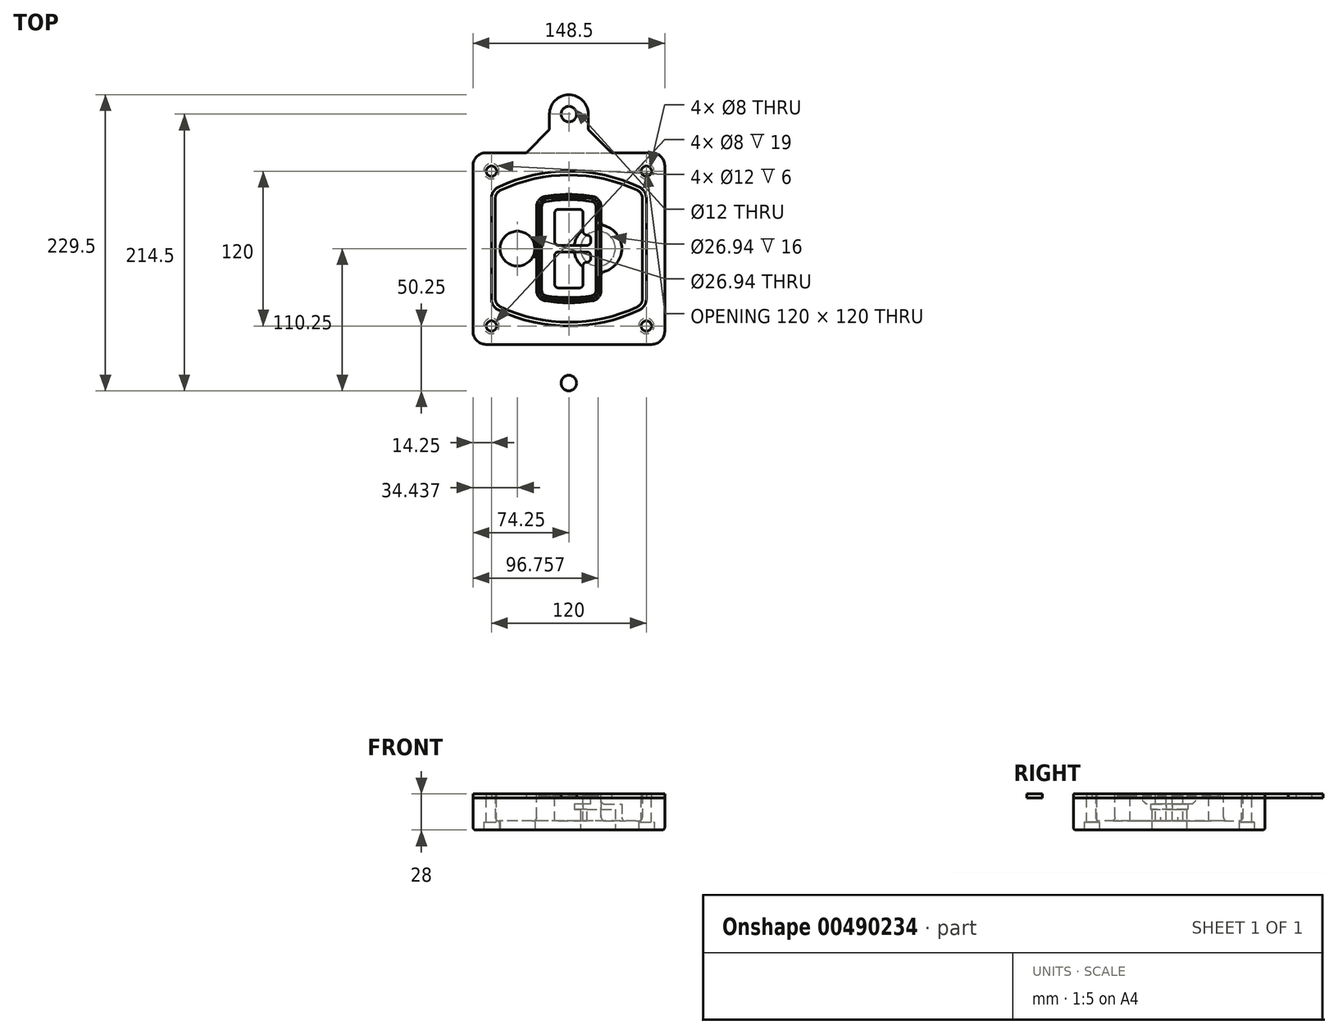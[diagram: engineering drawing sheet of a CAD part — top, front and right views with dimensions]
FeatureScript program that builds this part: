
annotation { "Feature Type Name" : "Feature", "Feature Type Description" : "" }
export const myFeature = defineFeature(function(context is Context, id is Id, definition is map)
    precondition{}
    {
        {
            var Q0;
            Q0=qCreatedBy(makeId("Top.planeOp"),FACE);
            var sketch = newSketch(context, id + "F0", { "sketchPlane" : qUnion([Q0])});
            skPoint(sketch, "E0.rect.middle", {"position": v(0, 0) * mm});
            skLineSegment(sketch, "E1.bottom", {"start": v(-64.25, -74.25) * mm, "end": v(64.25, -74.25) * mm});
            skLineSegment(sketch, "E1.top", {"start": v(-64.25, 74.25) * mm, "end": v(64.25, 74.25) * mm});
            skLineSegment(sketch, "E1.left", {"start": v(-74.25, -64.25) * mm, "end": v(-74.25, 64.25) * mm});
            skLineSegment(sketch, "E1.right", {"start": v(74.25, -64.25) * mm, "end": v(74.25, 64.25) * mm});
            skLineSegment(sketch, "E2", {"start": v(-74.25, 74.25) * mm, "end": v(74.25, -74.25) * mm, "construction": true});
            skLineSegment(sketch, "E3", {"start": v(74.25, 74.25) * mm, "end": v(-74.25, -74.25) * mm, "construction": true});
            skCircle(sketch, "E4", {"center": v(-60, 60) * mm, "radius": 4 * mm});
            skCircle(sketch, "E5", {"center": v(60, 60) * mm, "radius": 4 * mm});
            skCircle(sketch, "E6", {"center": v(60, -60) * mm, "radius": 4 * mm});
            skCircle(sketch, "E7", {"center": v(-60, -60) * mm, "radius": 4 * mm});
            skLineSegment(sketch, "E8", {"start": v(-60, 60) * mm, "end": v(60, 60) * mm, "construction": true});
            skLineSegment(sketch, "E9", {"start": v(60, 60) * mm, "end": v(60, -60) * mm, "construction": true});
            skLineSegment(sketch, "E10", {"start": v(60, -60) * mm, "end": v(-60, -60) * mm, "construction": true});
            skLineSegment(sketch, "E11", {"start": v(-60, -60) * mm, "end": v(-60, 60) * mm, "construction": true});
            skLineSegment(sketch, "E12", {"start": v(-60, 38.83) * mm, "end": v(-60, -38.83) * mm});
            skLineSegment(sketch, "E13", {"start": v(60, 38.83) * mm, "end": v(60, -38.83) * mm});
            skArc(sketch, "E14", {"start": v(54.26, 47.88) * mm, "mid": v(0, 60) * mm, "end": v(-54.26, 47.88) * mm});
            skArc(sketch, "E15", {"start": v(-54.26, -47.88) * mm, "mid": v(0, -60) * mm, "end": v(54.26, -47.88) * mm});
            skLineSegment(sketch, "E16", {"start": v(-60, 0) * mm, "end": v(60, 0) * mm, "construction": true});
            skPoint(sketch, "E17.visualSharp", {"position": v(-60, -45) * mm});
            skArc(sketch, "E17.filletArc", {"start": v(-60, -38.83) * mm, "mid": v(-58.44, -44.2) * mm, "end": v(-54.26, -47.88) * mm});
            skPoint(sketch, "E18.visualSharp", {"position": v(-60, 45) * mm});
            skArc(sketch, "E18.filletArc", {"start": v(-54.26, 47.88) * mm, "mid": v(-58.44, 44.2) * mm, "end": v(-60, 38.83) * mm});
            skPoint(sketch, "E19.visualSharp", {"position": v(60, 45) * mm});
            skArc(sketch, "E19.filletArc", {"start": v(60, 38.83) * mm, "mid": v(58.44, 44.2) * mm, "end": v(54.26, 47.88) * mm});
            skPoint(sketch, "E20.visualSharp", {"position": v(60, -45) * mm});
            skArc(sketch, "E20.filletArc", {"start": v(54.26, -47.88) * mm, "mid": v(58.44, -44.2) * mm, "end": v(60, -38.83) * mm});
            skPoint(sketch, "E21.visualSharp", {"position": v(-74.25, 74.25) * mm});
            skArc(sketch, "E21.filletArc", {"start": v(-64.25, 74.25) * mm, "mid": v(-71.32, 71.32) * mm, "end": v(-74.25, 64.25) * mm});
            skPoint(sketch, "E22.visualSharp", {"position": v(74.25, 74.25) * mm});
            skArc(sketch, "E22.filletArc", {"start": v(74.25, 64.25) * mm, "mid": v(71.32, 71.32) * mm, "end": v(64.25, 74.25) * mm});
            skPoint(sketch, "E23.visualSharp", {"position": v(74.25, -74.25) * mm});
            skArc(sketch, "E23.filletArc", {"start": v(64.25, -74.25) * mm, "mid": v(71.32, -71.32) * mm, "end": v(74.25, -64.25) * mm});
            skPoint(sketch, "E24.visualSharp", {"position": v(-74.25, -74.25) * mm});
            skArc(sketch, "E24.filletArc", {"start": v(-74.25, -64.25) * mm, "mid": v(-71.32, -71.32) * mm, "end": v(-64.25, -74.25) * mm});
            skArc(sketch, "E25.0", {"start": v(57, 38.83) * mm, "mid": v(55.9, 42.58) * mm, "end": v(52.98, 45.17) * mm});
            skLineSegment(sketch, "E25.1", {"start": v(57, 38.83) * mm, "end": v(57, -38.83) * mm});
            skArc(sketch, "E25.2", {"start": v(52.98, -45.17) * mm, "mid": v(55.9, -42.58) * mm, "end": v(57, -38.83) * mm});
            skArc(sketch, "E25.3", {"start": v(-52.98, -45.17) * mm, "mid": v(0, -57) * mm, "end": v(52.98, -45.17) * mm});
            skArc(sketch, "E25.4", {"start": v(-57, -38.83) * mm, "mid": v(-55.9, -42.58) * mm, "end": v(-52.98, -45.17) * mm});
            skArc(sketch, "E25.5", {"start": v(52.98, 45.17) * mm, "mid": v(0, 57) * mm, "end": v(-52.98, 45.17) * mm});
            skLineSegment(sketch, "E25.6", {"start": v(-57, 38.83) * mm, "end": v(-57, -38.83) * mm});
            skArc(sketch, "E25.7", {"start": v(-52.98, 45.17) * mm, "mid": v(-55.9, 42.58) * mm, "end": v(-57, 38.83) * mm});
            skArc(sketch, "E26.0", {"start": v(-55.96, 51.5) * mm, "mid": v(-61.82, 46.33) * mm, "end": v(-64, 38.83) * mm});
            skArc(sketch, "E26.1", {"start": v(55.96, 51.5) * mm, "mid": v(0, 64) * mm, "end": v(-55.96, 51.5) * mm});
            skArc(sketch, "E26.2", {"start": v(64, 38.83) * mm, "mid": v(61.82, 46.33) * mm, "end": v(55.96, 51.5) * mm});
            skLineSegment(sketch, "E26.3", {"start": v(64, 38.83) * mm, "end": v(64, -38.83) * mm});
            skArc(sketch, "E26.4", {"start": v(55.96, -51.5) * mm, "mid": v(61.82, -46.33) * mm, "end": v(64, -38.83) * mm});
            skLineSegment(sketch, "E26.5", {"start": v(-64, 38.83) * mm, "end": v(-64, -38.83) * mm});
            skArc(sketch, "E26.6", {"start": v(-55.96, -51.5) * mm, "mid": v(0, -64) * mm, "end": v(55.96, -51.5) * mm});
            skArc(sketch, "E26.7", {"start": v(-64, -38.83) * mm, "mid": v(-61.82, -46.33) * mm, "end": v(-55.96, -51.5) * mm});
            skSolve(sketch);
        }
        {
            var Q0;
            Q0=makeQuery(id+"F0.imprint","IMPRINT",FACE,{"disambiguationData":[TD([[makeQuery(id+"F0.imprint","IMPRINT",EDGE,{"derivedFrom":sQuery(id+"F0.wireOp",EDGE,"E1.bottom")}),1.0]])]});
            var Q1;
            Q1=makeQuery(id+"F0.imprint","IMPRINT",FACE,{"disambiguationData":[TD([[makeQuery(id+"F0.imprint","IMPRINT",EDGE,{"derivedFrom":sQuery(id+"F0.wireOp",EDGE,"E12")}),1.0]])]});
            var Q2;
            Q2=makeQuery(id+"F0.imprint","IMPRINT",FACE,{"disambiguationData":[TD([[makeQuery(id+"F0.imprint","IMPRINT",EDGE,{"derivedFrom":sQuery(id+"F0.wireOp",EDGE,"E25.0")}),1.0]])]});
            var Q3;
            Q3=makeQuery(id+"F0.imprint","IMPRINT",FACE,{"disambiguationData":[TD([[makeQuery(id+"F0.imprint","IMPRINT",EDGE,{"derivedFrom":sQuery(id+"F0.wireOp",EDGE,"E12")}),-1.0]])]});
            extrude(context, id + "F1", {"entities" : qUnion([Q0, Q1, Q2, Q3]), "oppositeDirection" : true, "depth" : 25 * mm});
        }
        {
            var Q0;
            Q0=makeQuery(id+"F0.imprint","IMPRINT",FACE,{"disambiguationData":[TD([[makeQuery(id+"F0.imprint","IMPRINT",EDGE,{"derivedFrom":sQuery(id+"F0.wireOp",EDGE,"E12")}),1.0]])]});
            extrude(context, id + "F2", {"entities" : qUnion([Q0]), "operationType" : NewBodyOperationType.ADD, "depth" : 3 * mm});
        }
        {
            var Q0;
            Q0=makeQuery(id+"F0.imprint","IMPRINT",FACE,{"disambiguationData":[TD([[makeQuery(id+"F0.imprint","IMPRINT",EDGE,{"derivedFrom":sQuery(id+"F0.wireOp",EDGE,"E25.0")}),1.0]])]});
            extrude(context, id + "F3", {"entities" : qUnion([Q0]), "operationType" : NewBodyOperationType.REMOVE, "oppositeDirection" : true, "depth" : 18 * mm});
        }
        {
            var Q0;
            Q0=makeQuery(id+"F2.opExtrude","CAP_FACE",FACE,{"disambiguationData":[OSD([sQuery(id+"F0.wireOp",EDGE,"E12"),sQuery(id+"F0.wireOp",EDGE,"E13"),sQuery(id+"F0.wireOp",EDGE,"E14"),sQuery(id+"F0.wireOp",EDGE,"E15"),sQuery(id+"F0.wireOp",EDGE,"E17.filletArc"),sQuery(id+"F0.wireOp",EDGE,"E18.filletArc"),sQuery(id+"F0.wireOp",EDGE,"E19.filletArc"),sQuery(id+"F0.wireOp",EDGE,"E20.filletArc"),sQuery(id+"F0.wireOp",EDGE,"E25.0"),sQuery(id+"F0.wireOp",EDGE,"E25.1"),sQuery(id+"F0.wireOp",EDGE,"E25.2"),sQuery(id+"F0.wireOp",EDGE,"E25.3"),sQuery(id+"F0.wireOp",EDGE,"E25.4"),sQuery(id+"F0.wireOp",EDGE,"E25.5"),sQuery(id+"F0.wireOp",EDGE,"E25.6"),sQuery(id+"F0.wireOp",EDGE,"E25.7")])],"isStart":false});
            var sketch = newSketch(context, id + "F4", { "sketchPlane" : qUnion([Q0])});
            skArc(sketch, "E27.0", {"start": v(-18.34, -40.45) * mm, "mid": v(0, -42) * mm, "end": v(18.34, -40.45) * mm});
            skArc(sketch, "E28.0", {"start": v(18.34, 40.45) * mm, "mid": v(0, 42) * mm, "end": v(-18.34, 40.45) * mm});
            skLineSegment(sketch, "E29", {"start": v(-25, 32.57) * mm, "end": v(-25, -32.57) * mm});
            skLineSegment(sketch, "E30", {"start": v(25, 32.57) * mm, "end": v(25, -32.57) * mm});
            skLineSegment(sketch, "E31", {"start": v(-25, 39.1) * mm, "end": v(25, 39.1) * mm, "construction": true});
            skLineSegment(sketch, "E32", {"start": v(-25, -39.1) * mm, "end": v(25, -39.1) * mm, "construction": true});
            skPoint(sketch, "E33.visualSharp", {"position": v(-25, 39.1) * mm});
            skArc(sketch, "E33.filletArc", {"start": v(-18.34, 40.45) * mm, "mid": v(-23.11, 37.73) * mm, "end": v(-25, 32.57) * mm});
            skPoint(sketch, "E34.visualSharp", {"position": v(25, 39.1) * mm});
            skArc(sketch, "E34.filletArc", {"start": v(25, 32.57) * mm, "mid": v(23.11, 37.73) * mm, "end": v(18.34, 40.45) * mm});
            skPoint(sketch, "E35.visualSharp", {"position": v(25, -39.1) * mm});
            skArc(sketch, "E35.filletArc", {"start": v(18.34, -40.45) * mm, "mid": v(23.11, -37.73) * mm, "end": v(25, -32.57) * mm});
            skPoint(sketch, "E36.visualSharp", {"position": v(-25, -39.1) * mm});
            skArc(sketch, "E36.filletArc", {"start": v(-25, -32.57) * mm, "mid": v(-23.11, -37.73) * mm, "end": v(-18.34, -40.45) * mm});
            skArc(sketch, "E37.0", {"start": v(52.98, 45.17) * mm, "mid": v(0, 57) * mm, "end": v(-52.98, 45.17) * mm});
            skArc(sketch, "E37.1", {"start": v(-52.98, 45.17) * mm, "mid": v(-55.9, 42.58) * mm, "end": v(-57, 38.83) * mm});
            skLineSegment(sketch, "E37.2", {"start": v(-57, 38.83) * mm, "end": v(-57, -38.83) * mm});
            skArc(sketch, "E37.3", {"start": v(-57, -38.83) * mm, "mid": v(-55.9, -42.58) * mm, "end": v(-52.98, -45.17) * mm});
            skArc(sketch, "E37.4", {"start": v(-52.98, -45.17) * mm, "mid": v(0, -57) * mm, "end": v(52.98, -45.17) * mm});
            skArc(sketch, "E37.5", {"start": v(52.98, -45.17) * mm, "mid": v(55.9, -42.58) * mm, "end": v(57, -38.83) * mm});
            skLineSegment(sketch, "E37.6", {"start": v(57, 38.83) * mm, "end": v(57, -38.83) * mm});
            skArc(sketch, "E37.7", {"start": v(57, 38.83) * mm, "mid": v(55.9, 42.58) * mm, "end": v(52.98, 45.17) * mm});
            skLineSegment(sketch, "E38.0", {"start": v(23, 32.57) * mm, "end": v(23, -32.57) * mm});
            skArc(sketch, "E38.1", {"start": v(18, -38.48) * mm, "mid": v(21.58, -36.44) * mm, "end": v(23, -32.57) * mm});
            skArc(sketch, "E38.2", {"start": v(-18, -38.48) * mm, "mid": v(0, -40) * mm, "end": v(18, -38.48) * mm});
            skArc(sketch, "E38.3", {"start": v(-23, -32.57) * mm, "mid": v(-21.58, -36.44) * mm, "end": v(-18, -38.48) * mm});
            skLineSegment(sketch, "E38.4", {"start": v(-23, 32.57) * mm, "end": v(-23, -32.57) * mm});
            skArc(sketch, "E38.5", {"start": v(23, 32.57) * mm, "mid": v(21.58, 36.44) * mm, "end": v(18, 38.48) * mm});
            skArc(sketch, "E38.6", {"start": v(-18, 38.48) * mm, "mid": v(-21.58, 36.44) * mm, "end": v(-23, 32.57) * mm});
            skArc(sketch, "E38.7", {"start": v(18, 38.48) * mm, "mid": v(0, 40) * mm, "end": v(-18, 38.48) * mm});
            skArc(sketch, "E39.0", {"start": v(21, 32.57) * mm, "mid": v(20.06, 35.15) * mm, "end": v(17.67, 36.5) * mm});
            skLineSegment(sketch, "E39.1", {"start": v(21, 32.57) * mm, "end": v(21, -32.57) * mm});
            skArc(sketch, "E39.2", {"start": v(17.67, -36.5) * mm, "mid": v(20.06, -35.15) * mm, "end": v(21, -32.57) * mm});
            skArc(sketch, "E39.3", {"start": v(-17.67, -36.5) * mm, "mid": v(0, -38) * mm, "end": v(17.67, -36.5) * mm});
            skArc(sketch, "E39.4", {"start": v(-21, -32.57) * mm, "mid": v(-20.06, -35.15) * mm, "end": v(-17.67, -36.5) * mm});
            skArc(sketch, "E39.5", {"start": v(17.67, 36.5) * mm, "mid": v(0, 38) * mm, "end": v(-17.67, 36.5) * mm});
            skLineSegment(sketch, "E39.6", {"start": v(-21, 32.57) * mm, "end": v(-21, -32.57) * mm});
            skArc(sketch, "E39.7", {"start": v(-17.67, 36.5) * mm, "mid": v(-20.06, 35.15) * mm, "end": v(-21, 32.57) * mm});
            skLineSegment(sketch, "E40", {"start": v(-25, 0) * mm, "end": v(25, 0) * mm, "construction": true});
            skLineSegment(sketch, "E41", {"start": v(-11, 5.5) * mm, "end": v(-11, 27.5) * mm});
            skLineSegment(sketch, "E42", {"start": v(-8, 30.5) * mm, "end": v(8, 30.5) * mm});
            skLineSegment(sketch, "E43", {"start": v(11, 27.5) * mm, "end": v(11, 13.5) * mm});
            skLineSegment(sketch, "E44", {"start": v(14, 10.5) * mm, "end": v(14, 10.5) * mm});
            skLineSegment(sketch, "E45", {"start": v(17, 7.5) * mm, "end": v(17, 5.5) * mm});
            skLineSegment(sketch, "E46", {"start": v(14, 2.5) * mm, "end": v(-8, 2.5) * mm});
            skPoint(sketch, "E47.visualSharp", {"position": v(-11, 30.5) * mm});
            skArc(sketch, "E47.filletArc", {"start": v(-8, 30.5) * mm, "mid": v(-10.12, 29.62) * mm, "end": v(-11, 27.5) * mm});
            skPoint(sketch, "E48.visualSharp", {"position": v(11, 30.5) * mm});
            skArc(sketch, "E48.filletArc", {"start": v(11, 27.5) * mm, "mid": v(10.12, 29.62) * mm, "end": v(8, 30.5) * mm});
            skPoint(sketch, "E49.visualSharp", {"position": v(11, 10.5) * mm});
            skArc(sketch, "E49.filletArc", {"start": v(11, 13.5) * mm, "mid": v(11.88, 11.38) * mm, "end": v(14, 10.5) * mm});
            skPoint(sketch, "E50.visualSharp", {"position": v(17, 10.5) * mm});
            skArc(sketch, "E50.filletArc", {"start": v(17, 7.5) * mm, "mid": v(16.12, 9.62) * mm, "end": v(14, 10.5) * mm});
            skPoint(sketch, "E51.visualSharp", {"position": v(17, 2.5) * mm});
            skArc(sketch, "E51.filletArc", {"start": v(14, 2.5) * mm, "mid": v(16.12, 3.38) * mm, "end": v(17, 5.5) * mm});
            skPoint(sketch, "E52.visualSharp", {"position": v(-11, 2.5) * mm});
            skArc(sketch, "E52.filletArc", {"start": v(-11, 5.5) * mm, "mid": v(-10.12, 3.38) * mm, "end": v(-8, 2.5) * mm});
            skLineSegment(sketch, "E53.0.MirrorCS", {"start": v(14, -2.5) * mm, "end": v(-8, -2.5) * mm});
            skArc(sketch, "E54.0.MirrorCS", {"start": v(-11, -5.5) * mm, "mid": v(-10.12, -3.38) * mm, "end": v(-8, -2.5) * mm});
            skLineSegment(sketch, "E55.0.MirrorCS", {"start": v(-11, -5.5) * mm, "end": v(-11, -27.5) * mm});
            skArc(sketch, "E56.0.MirrorCS", {"start": v(-8, -30.5) * mm, "mid": v(-10.12, -29.62) * mm, "end": v(-11, -27.5) * mm});
            skLineSegment(sketch, "E57.0.MirrorCS", {"start": v(-8, -30.5) * mm, "end": v(8, -30.5) * mm});
            skArc(sketch, "E58.0.MirrorCS", {"start": v(11, -27.5) * mm, "mid": v(10.12, -29.62) * mm, "end": v(8, -30.5) * mm});
            skLineSegment(sketch, "E59.0.MirrorCS", {"start": v(11, -27.5) * mm, "end": v(11, -13.5) * mm});
            skArc(sketch, "E60.0.MirrorCS", {"start": v(11, -13.5) * mm, "mid": v(11.88, -11.38) * mm, "end": v(14, -10.5) * mm});
            skArc(sketch, "E61.0.MirrorCS", {"start": v(17, -7.5) * mm, "mid": v(16.12, -9.62) * mm, "end": v(14, -10.5) * mm});
            skLineSegment(sketch, "E62.0.MirrorCS", {"start": v(17, -7.5) * mm, "end": v(17, -5.5) * mm});
            skArc(sketch, "E63.0.MirrorCS", {"start": v(14, -2.5) * mm, "mid": v(16.12, -3.38) * mm, "end": v(17, -5.5) * mm});
            skSolve(sketch);
        }
        {
            var Q0;
            Q0=makeQuery(id+"F4.imprint","IMPRINT",FACE,{"disambiguationData":[TD([[makeQuery(id+"F4.imprint","IMPRINT",EDGE,{"derivedFrom":sQuery(id+"F4.wireOp",EDGE,"E27.0")}),1.0]])]});
            var Q1;
            Q1=makeQuery(id+"F4.imprint","IMPRINT",FACE,{"disambiguationData":[TD([[makeQuery(id+"F4.imprint","IMPRINT",EDGE,{"derivedFrom":sQuery(id+"F4.wireOp",EDGE,"E38.0")}),-1.0]])]});
            var Q2;
            Q2=makeQuery(id+"F4.imprint","IMPRINT",FACE,{"disambiguationData":[TD([[makeQuery(id+"F4.imprint","IMPRINT",EDGE,{"derivedFrom":sQuery(id+"F4.wireOp",EDGE,"E39.0")}),1.0]])]});
            extrude(context, id + "F5", {"entities" : qUnion([Q0, Q1, Q2]), "operationType" : NewBodyOperationType.ADD, "endBound" : BoundingType.UP_TO_NEXT, "oppositeDirection" : true, "depth" : 25 * mm});
        }
        {
            var Q0;
            Q0=makeQuery(id+"F4.imprint","IMPRINT",FACE,{"disambiguationData":[TD([[makeQuery(id+"F4.imprint","IMPRINT",EDGE,{"derivedFrom":sQuery(id+"F4.wireOp",EDGE,"E38.0")}),-1.0]])]});
            extrude(context, id + "F6", {"entities" : qUnion([Q0]), "operationType" : NewBodyOperationType.REMOVE, "oppositeDirection" : true, "depth" : 2 * mm});
        }
        {
            var Q0;
            Q0=makeQuery(id+"F1.opExtrude","CAP_FACE",FACE,{"disambiguationData":[OSD([sQuery(id+"F0.wireOp",EDGE,"E1.bottom"),sQuery(id+"F0.wireOp",EDGE,"E1.top"),sQuery(id+"F0.wireOp",EDGE,"E1.left"),sQuery(id+"F0.wireOp",EDGE,"E1.right"),sQuery(id+"F0.wireOp",EDGE,"E4"),sQuery(id+"F0.wireOp",EDGE,"E5"),sQuery(id+"F0.wireOp",EDGE,"E6"),sQuery(id+"F0.wireOp",EDGE,"E7"),sQuery(id+"F0.wireOp",EDGE,"E21.filletArc"),sQuery(id+"F0.wireOp",EDGE,"E22.filletArc"),sQuery(id+"F0.wireOp",EDGE,"E23.filletArc"),sQuery(id+"F0.wireOp",EDGE,"E24.filletArc")])],"isStart":false});
            var sketch = newSketch(context, id + "F7", { "sketchPlane" : qUnion([Q0])});
            skCircle(sketch, "E64", {"center": v(22.5, 0) * mm, "radius": 13.47 * mm});
            skCircle(sketch, "E65", {"center": v(-39.81, 0) * mm, "radius": 13.47 * mm});
            skLineSegment(sketch, "E66", {"start": v(74.25, 0) * mm, "end": v(-74.25, 0) * mm});
            skCircle(sketch, "E67", {"center": v(22.5, 0) * mm, "radius": 18.47 * mm});
            skCircle(sketch, "E68", {"center": v(60, -60) * mm, "radius": 6 * mm});
            skCircle(sketch, "E69", {"center": v(-60, -60) * mm, "radius": 6 * mm});
            skCircle(sketch, "E70", {"center": v(-60, 60) * mm, "radius": 6 * mm});
            skCircle(sketch, "E71", {"center": v(60, 60) * mm, "radius": 6 * mm});
            skSolve(sketch);
        }
        {
            var Q0;
            {var subQ1=sQuery(id+"F7.wireOp",EDGE,"E66");var subQ4=sQuery(id+"F7.wireOp",EDGE,"E64");var subQ6=makeQuery(id+"F7.imprint","INTERSECT",VERTEX,{"disambiguationData":[OD(0.0)],"derivedFrom":[subQ4,subQ1]});Q0=makeQuery(id+"F7.imprint","IMPRINT",FACE,{"disambiguationData":[TD([[makeQuery(id+"F7.imprint","IMPRINT",EDGE,{"disambiguationData":[TD([[subQ6,-1.0]])],"derivedFrom":subQ4}),-1.0]])]});}
            var Q1;
            {var subQ0=sQuery(id+"F7.wireOp",EDGE,"E66");var subQ1=sQuery(id+"F7.wireOp",EDGE,"E64");var subQ3=makeQuery(id+"F7.imprint","INTERSECT",VERTEX,{"disambiguationData":[OD(0.0)],"derivedFrom":[subQ1,subQ0]});Q1=makeQuery(id+"F7.imprint","IMPRINT",FACE,{"disambiguationData":[TD([[makeQuery(id+"F7.imprint","IMPRINT",EDGE,{"disambiguationData":[TD([[subQ3,-1.0]])],"derivedFrom":subQ1}),1.0]])]});}
            var Q2;
            {var subQ0=sQuery(id+"F7.wireOp",EDGE,"E66");var subQ1=sQuery(id+"F7.wireOp",EDGE,"E64");var subQ3=makeQuery(id+"F7.imprint","INTERSECT",VERTEX,{"disambiguationData":[OD(0.0)],"derivedFrom":[subQ1,subQ0]});Q2=makeQuery(id+"F7.imprint","IMPRINT",FACE,{"disambiguationData":[TD([[makeQuery(id+"F7.imprint","IMPRINT",EDGE,{"disambiguationData":[TD([[subQ3,1.0]])],"derivedFrom":subQ1}),1.0]])]});}
            var Q3;
            {var subQ1=sQuery(id+"F7.wireOp",EDGE,"E66");var subQ4=sQuery(id+"F7.wireOp",EDGE,"E64");var subQ6=makeQuery(id+"F7.imprint","INTERSECT",VERTEX,{"disambiguationData":[OD(0.0)],"derivedFrom":[subQ4,subQ1]});Q3=makeQuery(id+"F7.imprint","IMPRINT",FACE,{"disambiguationData":[TD([[makeQuery(id+"F7.imprint","IMPRINT",EDGE,{"disambiguationData":[TD([[subQ6,1.0]])],"derivedFrom":subQ4}),-1.0]])]});}
            extrude(context, id + "F8", {"entities" : qUnion([Q0, Q1, Q2, Q3]), "operationType" : NewBodyOperationType.ADD, "oppositeDirection" : true, "depth" : 20 * mm});
        }
        {
            var Q0;
            {var subQ0=sQuery(id+"F7.wireOp",EDGE,"E66");var subQ1=sQuery(id+"F7.wireOp",EDGE,"E64");var subQ3=makeQuery(id+"F7.imprint","INTERSECT",VERTEX,{"disambiguationData":[OD(0.0)],"derivedFrom":[subQ1,subQ0]});Q0=makeQuery(id+"F7.imprint","IMPRINT",FACE,{"disambiguationData":[TD([[makeQuery(id+"F7.imprint","IMPRINT",EDGE,{"disambiguationData":[TD([[subQ3,-1.0]])],"derivedFrom":subQ1}),1.0]])]});}
            var Q1;
            {var subQ0=sQuery(id+"F7.wireOp",EDGE,"E66");var subQ1=sQuery(id+"F7.wireOp",EDGE,"E64");var subQ3=makeQuery(id+"F7.imprint","INTERSECT",VERTEX,{"disambiguationData":[OD(0.0)],"derivedFrom":[subQ1,subQ0]});Q1=makeQuery(id+"F7.imprint","IMPRINT",FACE,{"disambiguationData":[TD([[makeQuery(id+"F7.imprint","IMPRINT",EDGE,{"disambiguationData":[TD([[subQ3,1.0]])],"derivedFrom":subQ1}),1.0]])]});}
            extrude(context, id + "F9", {"entities" : qUnion([Q0, Q1]), "operationType" : NewBodyOperationType.REMOVE, "oppositeDirection" : true, "depth" : 16 * mm});
        }
        {
            var Q0;
            {var subQ0=sQuery(id+"F7.wireOp",EDGE,"E66");var subQ1=sQuery(id+"F7.wireOp",EDGE,"E65");var subQ3=makeQuery(id+"F7.imprint","INTERSECT",VERTEX,{"disambiguationData":[OD(0.0)],"derivedFrom":[subQ1,subQ0]});Q0=makeQuery(id+"F7.imprint","IMPRINT",FACE,{"disambiguationData":[TD([[makeQuery(id+"F7.imprint","IMPRINT",EDGE,{"disambiguationData":[TD([[subQ3,-1.0]])],"derivedFrom":subQ1}),1.0]])]});}
            var Q1;
            {var subQ0=sQuery(id+"F7.wireOp",EDGE,"E66");var subQ1=sQuery(id+"F7.wireOp",EDGE,"E65");var subQ3=makeQuery(id+"F7.imprint","INTERSECT",VERTEX,{"disambiguationData":[OD(0.0)],"derivedFrom":[subQ1,subQ0]});Q1=makeQuery(id+"F7.imprint","IMPRINT",FACE,{"disambiguationData":[TD([[makeQuery(id+"F7.imprint","IMPRINT",EDGE,{"disambiguationData":[TD([[subQ3,1.0]])],"derivedFrom":subQ1}),1.0]])]});}
            extrude(context, id + "F10", {"entities" : qUnion([Q0, Q1]), "operationType" : NewBodyOperationType.REMOVE, "oppositeDirection" : true, "depth" : 25 * mm});
        }
        {
            var Q0;
            Q0=makeQuery(id+"F7.imprint","IMPRINT",FACE,{"disambiguationData":[TD([[makeQuery(id+"F7.imprint","IMPRINT",EDGE,{"derivedFrom":sQuery(id+"F7.wireOp",EDGE,"E68")}),1.0]])]});
            var Q1;
            Q1=makeQuery(id+"F7.imprint","IMPRINT",FACE,{"disambiguationData":[TD([[makeQuery(id+"F7.imprint","IMPRINT",EDGE,{"derivedFrom":makeQuery(id+"F1.opExtrude","CAP_EDGE",EDGE,{"disambiguationData":[OSD([sQuery(id+"F0.wireOp",EDGE,"E5")])],"isStart":false})}),-1.0]])]});
            var Q2;
            Q2=makeQuery(id+"F7.imprint","IMPRINT",FACE,{"disambiguationData":[TD([[makeQuery(id+"F7.imprint","IMPRINT",EDGE,{"derivedFrom":sQuery(id+"F7.wireOp",EDGE,"E69")}),1.0]])]});
            var Q3;
            Q3=makeQuery(id+"F7.imprint","IMPRINT",FACE,{"disambiguationData":[TD([[makeQuery(id+"F7.imprint","IMPRINT",EDGE,{"derivedFrom":makeQuery(id+"F1.opExtrude","CAP_EDGE",EDGE,{"disambiguationData":[OSD([sQuery(id+"F0.wireOp",EDGE,"E4")])],"isStart":false})}),-1.0]])]});
            var Q4;
            Q4=makeQuery(id+"F7.imprint","IMPRINT",FACE,{"disambiguationData":[TD([[makeQuery(id+"F7.imprint","IMPRINT",EDGE,{"derivedFrom":sQuery(id+"F7.wireOp",EDGE,"E70")}),1.0]])]});
            var Q5;
            Q5=makeQuery(id+"F7.imprint","IMPRINT",FACE,{"disambiguationData":[TD([[makeQuery(id+"F7.imprint","IMPRINT",EDGE,{"derivedFrom":makeQuery(id+"F1.opExtrude","CAP_EDGE",EDGE,{"disambiguationData":[OSD([sQuery(id+"F0.wireOp",EDGE,"E7")])],"isStart":false})}),-1.0]])]});
            var Q6;
            Q6=makeQuery(id+"F7.imprint","IMPRINT",FACE,{"disambiguationData":[TD([[makeQuery(id+"F7.imprint","IMPRINT",EDGE,{"derivedFrom":sQuery(id+"F7.wireOp",EDGE,"E71")}),1.0]])]});
            var Q7;
            Q7=makeQuery(id+"F7.imprint","IMPRINT",FACE,{"disambiguationData":[TD([[makeQuery(id+"F7.imprint","IMPRINT",EDGE,{"derivedFrom":makeQuery(id+"F1.opExtrude","CAP_EDGE",EDGE,{"disambiguationData":[OSD([sQuery(id+"F0.wireOp",EDGE,"E6")])],"isStart":false})}),-1.0]])]});
            extrude(context, id + "F11", {"entities" : qUnion([Q0, Q1, Q2, Q3, Q4, Q5, Q6, Q7]), "operationType" : NewBodyOperationType.REMOVE, "oppositeDirection" : true, "depth" : 6 * mm});
        }
        {
            var Q0;
            Q0=makeQuery(id+"F9.boolean.opBoolean","COPY",FACE,{"derivedFrom":makeQuery(id+"F9.opExtrude","CAP_FACE",FACE,{"disambiguationData":[OSD([sQuery(id+"F7.wireOp",EDGE,"E64")])],"isStart":false})});
            var sketch = newSketch(context, id + "F12", { "sketchPlane" : qUnion([Q0])});
            skArc(sketch, "E72.0", {"start": v(11, 14.45) * mm, "mid": v(6.45, 9.13) * mm, "end": v(4.2, 2.5) * mm});
            skArc(sketch, "E72.1", {"start": v(4.2, -2.5) * mm, "mid": v(6.45, -9.13) * mm, "end": v(11, -14.45) * mm});
            skLineSegment(sketch, "E73", {"start": v(4.2, -2.5) * mm, "end": v(14, -2.5) * mm});
            skLineSegment(sketch, "E74.0", {"start": v(14, 2.5) * mm, "end": v(4.2, 2.5) * mm});
            skArc(sketch, "E74.1", {"start": v(14, 2.5) * mm, "mid": v(16.12, 3.38) * mm, "end": v(17, 5.5) * mm});
            skLineSegment(sketch, "E74.2", {"start": v(17, 7.5) * mm, "end": v(17, 5.5) * mm});
            skArc(sketch, "E74.3", {"start": v(17, 7.5) * mm, "mid": v(16.12, 9.62) * mm, "end": v(14, 10.5) * mm});
            skArc(sketch, "E74.4", {"start": v(11, 13.5) * mm, "mid": v(11.88, 11.38) * mm, "end": v(14, 10.5) * mm});
            skLineSegment(sketch, "E74.5", {"start": v(11, 14.45) * mm, "end": v(11, 13.5) * mm});
            skLineSegment(sketch, "E74.7", {"start": v(14, -2.5) * mm, "end": v(4.2, -2.5) * mm});
            skArc(sketch, "E74.8", {"start": v(14, -2.5) * mm, "mid": v(16.12, -3.38) * mm, "end": v(17, -5.5) * mm});
            skLineSegment(sketch, "E74.9", {"start": v(17, -7.5) * mm, "end": v(17, -5.5) * mm});
            skArc(sketch, "E74.10", {"start": v(17, -7.5) * mm, "mid": v(16.12, -9.62) * mm, "end": v(14, -10.5) * mm});
            skArc(sketch, "E74.11", {"start": v(11, -13.5) * mm, "mid": v(11.88, -11.38) * mm, "end": v(14, -10.5) * mm});
            skLineSegment(sketch, "E74.12", {"start": v(11, -14.45) * mm, "end": v(11, -13.5) * mm});
            skPoint(sketch, "E75.orphan", {"position": v(11, -27.5) * mm});
            skPoint(sketch, "E76.orphan", {"position": v(-8, -2.5) * mm});
            skPoint(sketch, "E77.orphan", {"position": v(-8, 2.5) * mm});
            skPoint(sketch, "E78.orphan", {"position": v(11, 27.5) * mm});
            skSolve(sketch);
        }
        {
            var Q0;
            {var subQ7=sQuery(id+"F12.wireOp",EDGE,"E72.0");var subQ14=sQuery(id+"F12.wireOp",EDGE,"E72.1");var subQ16=sQuery(id+"F12.wireOp",EDGE,"E74.1");var subQ18=sQuery(id+"F12.wireOp",EDGE,"E74.8");Q0=qUnion([makeQuery(id+"F12.imprint","IMPRINT",FACE,{"disambiguationData":[TD([[makeQuery(id+"F12.imprint","IMPRINT",EDGE,{"derivedFrom":subQ7}),1.0]])]}),makeQuery(id+"F12.imprint","IMPRINT",FACE,{"disambiguationData":[TD([[makeQuery(id+"F12.imprint","IMPRINT",EDGE,{"derivedFrom":subQ14}),1.0]])]}),makeQuery(id+"F12.imprint","IMPRINT",FACE,{"disambiguationData":[TD([[makeQuery(id+"F12.imprint","IMPRINT",EDGE,{"derivedFrom":subQ16}),1.0]])]}),makeQuery(id+"F12.imprint","IMPRINT",FACE,{"disambiguationData":[TD([[makeQuery(id+"F12.imprint","IMPRINT",EDGE,{"derivedFrom":subQ18}),-1.0]])]})]);}
            var Q1;
            Q1=makeQuery(id+"F5.boolean.opBoolean","SPLIT",FACE,{"disambiguationData":[TD([makeQuery(id+"F5.opExtrude","SWEPT_FACE",FACE,{"disambiguationData":[OSD([sQuery(id+"F4.wireOp",EDGE,"E41")])]})])],"derivedFrom":makeQuery(id+"F3.boolean.opBoolean","COPY",FACE,{"derivedFrom":makeQuery(id+"F3.opExtrude","CAP_FACE",FACE,{"disambiguationData":[OSD([sQuery(id+"F0.wireOp",EDGE,"E25.0"),sQuery(id+"F0.wireOp",EDGE,"E25.1"),sQuery(id+"F0.wireOp",EDGE,"E25.2"),sQuery(id+"F0.wireOp",EDGE,"E25.3"),sQuery(id+"F0.wireOp",EDGE,"E25.4"),sQuery(id+"F0.wireOp",EDGE,"E25.5"),sQuery(id+"F0.wireOp",EDGE,"E25.6"),sQuery(id+"F0.wireOp",EDGE,"E25.7")])],"isStart":false})})});
            extrude(context, id + "F13", {"entities" : qUnion([Q0]), "operationType" : NewBodyOperationType.REMOVE, "endBound" : BoundingType.UP_TO_SURFACE, "endBoundEntityFace" : qUnion([Q1]), "depth" : 25 * mm});
        }
        {
            var Q0;
            Q0=makeQuery(id+"F3.boolean.opBoolean","COPY",EDGE,{"derivedFrom":makeQuery(id+"F3.opExtrude","CAP_EDGE",EDGE,{"disambiguationData":[OSD([sQuery(id+"F0.wireOp",EDGE,"E25.6")])],"isStart":false})});
            var Q1;
            Q1=makeQuery(id+"F8.boolean.opBoolean","INTERSECT",EDGE,{"derivedFrom":[makeQuery(id+"F5.opExtrude","SWEPT_FACE",FACE,{"disambiguationData":[OSD([sQuery(id+"F4.wireOp",EDGE,"E30")])]}),makeQuery(id+"F8.opExtrude","CAP_FACE",FACE,{"disambiguationData":[OSD([sQuery(id+"F7.wireOp",EDGE,"E67")])],"isStart":false})]});
            var Q2;
            Q2=makeQuery(id+"F8.boolean.opBoolean","INTERSECT",EDGE,{"disambiguationData":[OD(1.0)],"derivedFrom":[makeQuery(id+"F5.opExtrude","SWEPT_FACE",FACE,{"disambiguationData":[OSD([sQuery(id+"F4.wireOp",EDGE,"E30")])]}),makeQuery(id+"F8.opExtrude","SWEPT_FACE",FACE,{"disambiguationData":[OSD([sQuery(id+"F7.wireOp",EDGE,"E67")])]})]});
            var Q3;
            {var subQ0=sQuery(id+"F4.wireOp",EDGE,"E30");Q3=makeQuery(id+"F8.boolean.opBoolean","SPLIT",EDGE,{"disambiguationData":[TD([makeQuery(id+"F5.opExtrude","SWEPT_FACE",FACE,{"disambiguationData":[OSD([sQuery(id+"F4.wireOp",EDGE,"E35.filletArc")])]})])],"derivedFrom":makeQuery(id+"F5.opExtrude","CAP_EDGE",EDGE,{"disambiguationData":[OSD([subQ0])],"isStart":false})});}
            var Q4;
            {var subQ0=sQuery(id+"F0.wireOp",EDGE,"E25.7");var subQ1=sQuery(id+"F0.wireOp",EDGE,"E25.1");var subQ2=sQuery(id+"F0.wireOp",EDGE,"E25.6");var subQ3=sQuery(id+"F0.wireOp",EDGE,"E25.5");var subQ4=sQuery(id+"F0.wireOp",EDGE,"E25.4");var subQ5=sQuery(id+"F0.wireOp",EDGE,"E25.0");var subQ6=sQuery(id+"F0.wireOp",EDGE,"E25.2");var subQ7=sQuery(id+"F0.wireOp",EDGE,"E25.3");Q4=makeQuery(id+"F8.boolean.opBoolean","INTERSECT",EDGE,{"derivedFrom":[makeQuery(id+"F5.boolean.opBoolean","SPLIT",FACE,{"disambiguationData":[TD([makeQuery(id+"F2.opExtrude","SWEPT_FACE",FACE,{"disambiguationData":[OSD([subQ5])]})])],"derivedFrom":makeQuery(id+"F3.boolean.opBoolean","COPY",FACE,{"derivedFrom":makeQuery(id+"F3.opExtrude","CAP_FACE",FACE,{"disambiguationData":[OSD([subQ5,subQ1,subQ6,subQ7,subQ4,subQ3,subQ2,subQ0])],"isStart":false})})}),makeQuery(id+"F8.opExtrude","SWEPT_FACE",FACE,{"disambiguationData":[OSD([sQuery(id+"F7.wireOp",EDGE,"E67")])]})]});}
            var Q5;
            Q5=makeQuery(id+"F8.boolean.opBoolean","INTERSECT",EDGE,{"disambiguationData":[OD(0.0)],"derivedFrom":[makeQuery(id+"F5.opExtrude","SWEPT_FACE",FACE,{"disambiguationData":[OSD([sQuery(id+"F4.wireOp",EDGE,"E30")])]}),makeQuery(id+"F8.opExtrude","SWEPT_FACE",FACE,{"disambiguationData":[OSD([sQuery(id+"F7.wireOp",EDGE,"E67")])]})]});
            fillet(context, id + "F14", {"entities" : qUnion([Q0, Q1, Q2, Q3, Q4, Q5]), "radius" : 3 * mm, "tangentPropagation" : true, "allowEdgeOverflow" : false});
        }
        {
            var Q0;
            Q0=makeQuery(id+"F1.opExtrude","CAP_EDGE",EDGE,{"disambiguationData":[OSD([sQuery(id+"F0.wireOp",EDGE,"E1.bottom")])],"isStart":false});
            fillet(context, id + "F15", {"entities" : qUnion([Q0]), "radius" : 2 * mm, "tangentPropagation" : true, "allowEdgeOverflow" : false});
        }
        {
            var Q0;
            {var subQ0=sQuery(id+"F0.wireOp",EDGE,"E21.filletArc");var subQ1=sQuery(id+"F0.wireOp",EDGE,"E7");var subQ2=sQuery(id+"F0.wireOp",EDGE,"E6");var subQ3=sQuery(id+"F0.wireOp",EDGE,"E5");var subQ4=sQuery(id+"F0.wireOp",EDGE,"E4");var subQ5=sQuery(id+"F0.wireOp",EDGE,"E22.filletArc");var subQ6=sQuery(id+"F0.wireOp",EDGE,"E1.bottom");var subQ7=sQuery(id+"F0.wireOp",EDGE,"E1.right");var subQ8=sQuery(id+"F0.wireOp",EDGE,"E1.top");var subQ9=sQuery(id+"F0.wireOp",EDGE,"E1.left");var subQ10=sQuery(id+"F0.wireOp",EDGE,"E23.filletArc");var subQ11=sQuery(id+"F0.wireOp",EDGE,"E24.filletArc");Q0=makeQuery(id+"F2.boolean.opBoolean","SPLIT",FACE,{"disambiguationData":[TD([makeQuery(id+"F1.opExtrude","SWEPT_FACE",FACE,{"disambiguationData":[OSD([subQ6])]})])],"derivedFrom":makeQuery(id+"F1.opExtrude","CAP_FACE",FACE,{"disambiguationData":[OSD([subQ6,subQ8,subQ9,subQ7,subQ4,subQ3,subQ2,subQ1,subQ0,subQ5,subQ10,subQ11])],"isStart":true})});}
            var sketch = newSketch(context, id + "F16", { "sketchPlane" : qUnion([Q0])});
            skLineSegment(sketch, "E79", {"start": v(0, 74.25) * mm, "end": v(0, 104.25) * mm, "construction": true});
            skArc(sketch, "E80", {"start": v(15, 104.25) * mm, "mid": v(0, 119.25) * mm, "end": v(-15, 104.25) * mm});
            skLineSegment(sketch, "E81", {"start": v(15, 104.25) * mm, "end": v(15, 92.25) * mm});
            skLineSegment(sketch, "E82", {"start": v(-15, 104.25) * mm, "end": v(-15, 92.25) * mm});
            skLineSegment(sketch, "E83", {"start": v(15, 92.25) * mm, "end": v(33, 74.25) * mm});
            skLineSegment(sketch, "E84", {"start": v(-15, 92.25) * mm, "end": v(-33, 74.25) * mm});
            skCircle(sketch, "E85", {"center": v(0, 104.25) * mm, "radius": 6 * mm});
            skLineSegment(sketch, "E86", {"start": v(-74.25, 0) * mm, "end": v(74.25, 0) * mm, "construction": true});
            skLineSegment(sketch, "E87.MirrorCS", {"start": v(0, -74.25) * mm, "end": v(0, -104.25) * mm, "construction": true});
            skCircle(sketch, "E88.MirrorC", {"center": v(0, -104.25) * mm, "radius": 6 * mm});
            skLineSegment(sketch, "E89.MirrorCS", {"start": v(-15, -92.25) * mm, "end": v(-33, -74.25) * mm});
            skArc(sketch, "E90.MirrorCS", {"start": v(15, -104.25) * mm, "mid": v(0, -119.25) * mm, "end": v(-15, -104.25) * mm});
            skLineSegment(sketch, "E91.MirrorCS", {"start": v(15, -92.25) * mm, "end": v(33, -74.25) * mm});
            skLineSegment(sketch, "E92.MirrorCS", {"start": v(-15, -104.25) * mm, "end": v(-15, -92.25) * mm});
            skLineSegment(sketch, "E93.MirrorCS", {"start": v(15, -104.25) * mm, "end": v(15, -92.25) * mm});
            skSolve(sketch);
        }
        {
            var Q0;
            Q0=makeQuery(id+"F16.imprint","IMPRINT",FACE,{"disambiguationData":[TD([[makeQuery(id+"F16.imprint","IMPRINT",EDGE,{"derivedFrom":sQuery(id+"F16.wireOp",EDGE,"E88.MirrorC")}),1.0]])]});
            var Q1;
            Q1=makeQuery(id+"F16.imprint","IMPRINT",FACE,{"disambiguationData":[TD([[makeQuery(id+"F16.imprint","IMPRINT",EDGE,{"derivedFrom":makeQuery(id+"F1.opExtrude","CAP_EDGE",EDGE,{"disambiguationData":[OSD([sQuery(id+"F0.wireOp",EDGE,"E1.left")])],"isStart":true})}),-1.0]])]});
            var Q2;
            Q2=makeQuery(id+"F16.imprint","IMPRINT",FACE,{"disambiguationData":[TD([[makeQuery(id+"F16.imprint","IMPRINT",EDGE,{"derivedFrom":sQuery(id+"F16.wireOp",EDGE,"E80")}),1.0]])]});
            var Q3;
            Q3=makeQuery(id+"F2.opExtrude","CAP_FACE",FACE,{"disambiguationData":[OSD([sQuery(id+"F0.wireOp",EDGE,"E12"),sQuery(id+"F0.wireOp",EDGE,"E13"),sQuery(id+"F0.wireOp",EDGE,"E14"),sQuery(id+"F0.wireOp",EDGE,"E15"),sQuery(id+"F0.wireOp",EDGE,"E17.filletArc"),sQuery(id+"F0.wireOp",EDGE,"E18.filletArc"),sQuery(id+"F0.wireOp",EDGE,"E19.filletArc"),sQuery(id+"F0.wireOp",EDGE,"E20.filletArc"),sQuery(id+"F0.wireOp",EDGE,"E25.0"),sQuery(id+"F0.wireOp",EDGE,"E25.1"),sQuery(id+"F0.wireOp",EDGE,"E25.2"),sQuery(id+"F0.wireOp",EDGE,"E25.3"),sQuery(id+"F0.wireOp",EDGE,"E25.4"),sQuery(id+"F0.wireOp",EDGE,"E25.5"),sQuery(id+"F0.wireOp",EDGE,"E25.6"),sQuery(id+"F0.wireOp",EDGE,"E25.7")])],"isStart":false});
            extrude(context, id + "F17", {"entities" : qUnion([Q0, Q1, Q2]), "endBound" : BoundingType.UP_TO_SURFACE, "endBoundEntityFace" : qUnion([Q3]), "depth" : 25 * mm});
        }
    });
